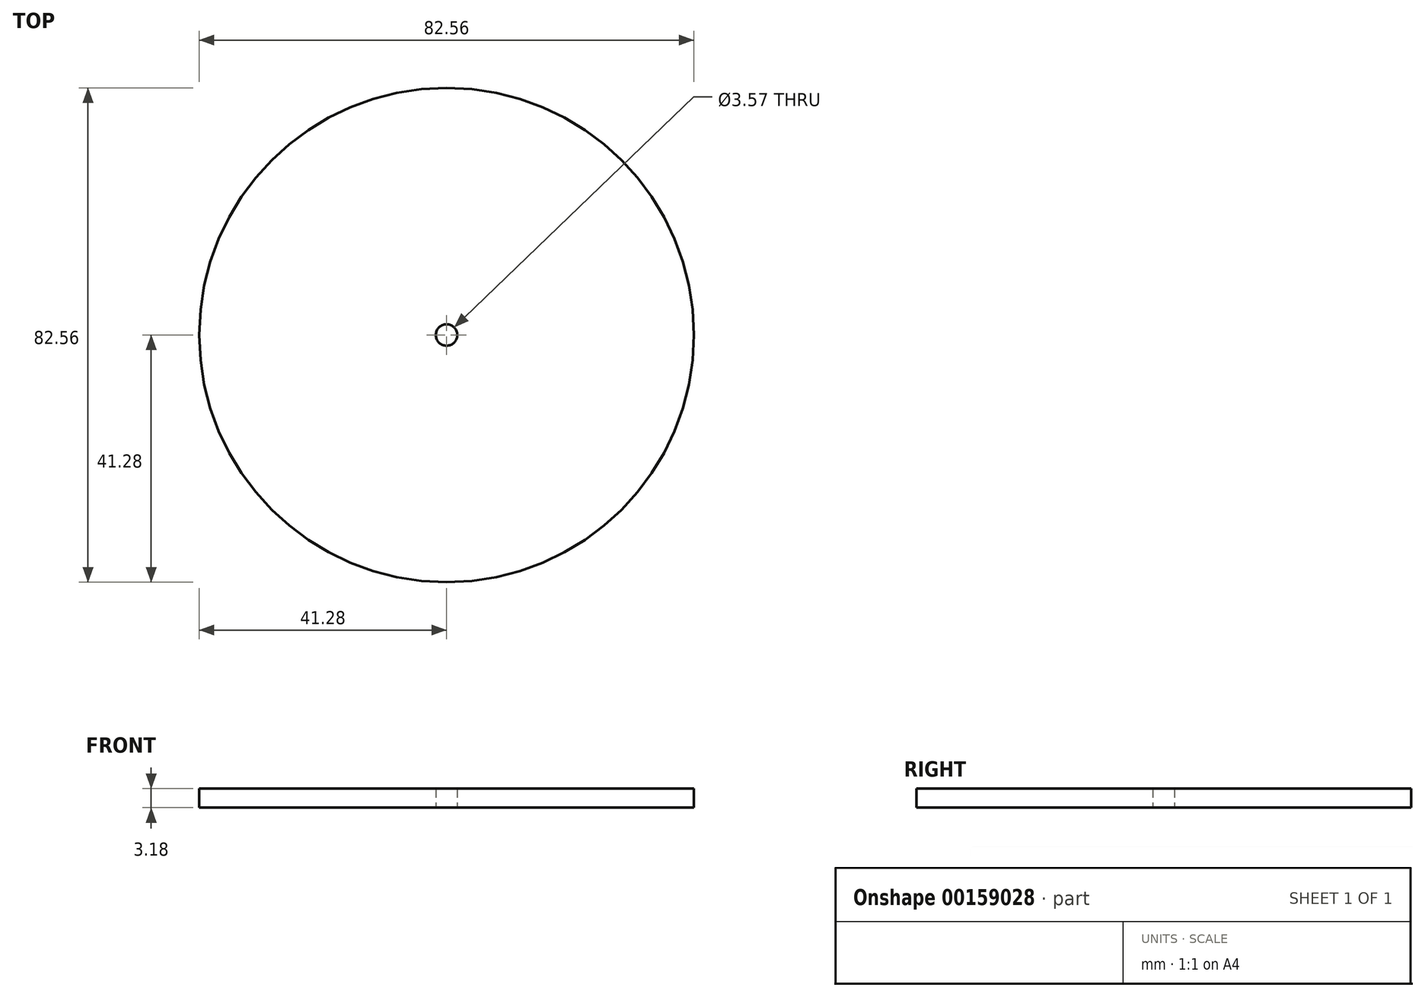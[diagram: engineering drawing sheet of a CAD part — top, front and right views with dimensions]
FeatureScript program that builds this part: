
annotation { "Feature Type Name" : "Feature", "Feature Type Description" : "" }
export const myFeature = defineFeature(function(context is Context, id is Id, definition is map)
    precondition{}
    {
        {
            var Q0;
            Q0=qCreatedBy(makeId("Top.planeOp"),FACE);
            var sketch = newSketch(context, id + "F0", { "sketchPlane" : qUnion([Q0])});
            skCircle(sketch, "E0", {"center": v(0, 0) * mm, "radius": 41.28 * mm});
            skCircle(sketch, "E1", {"center": v(0, 0) * mm, "radius": 1.79 * mm});
            skSolve(sketch);
        }
        {
            var Q0;
            Q0 = qSketchRegion(id + "F0", true);
            extrude(context, id + "F1", {"entities" : qUnion([Q0]), "depth" : 3.17 * mm});
        }
    });
